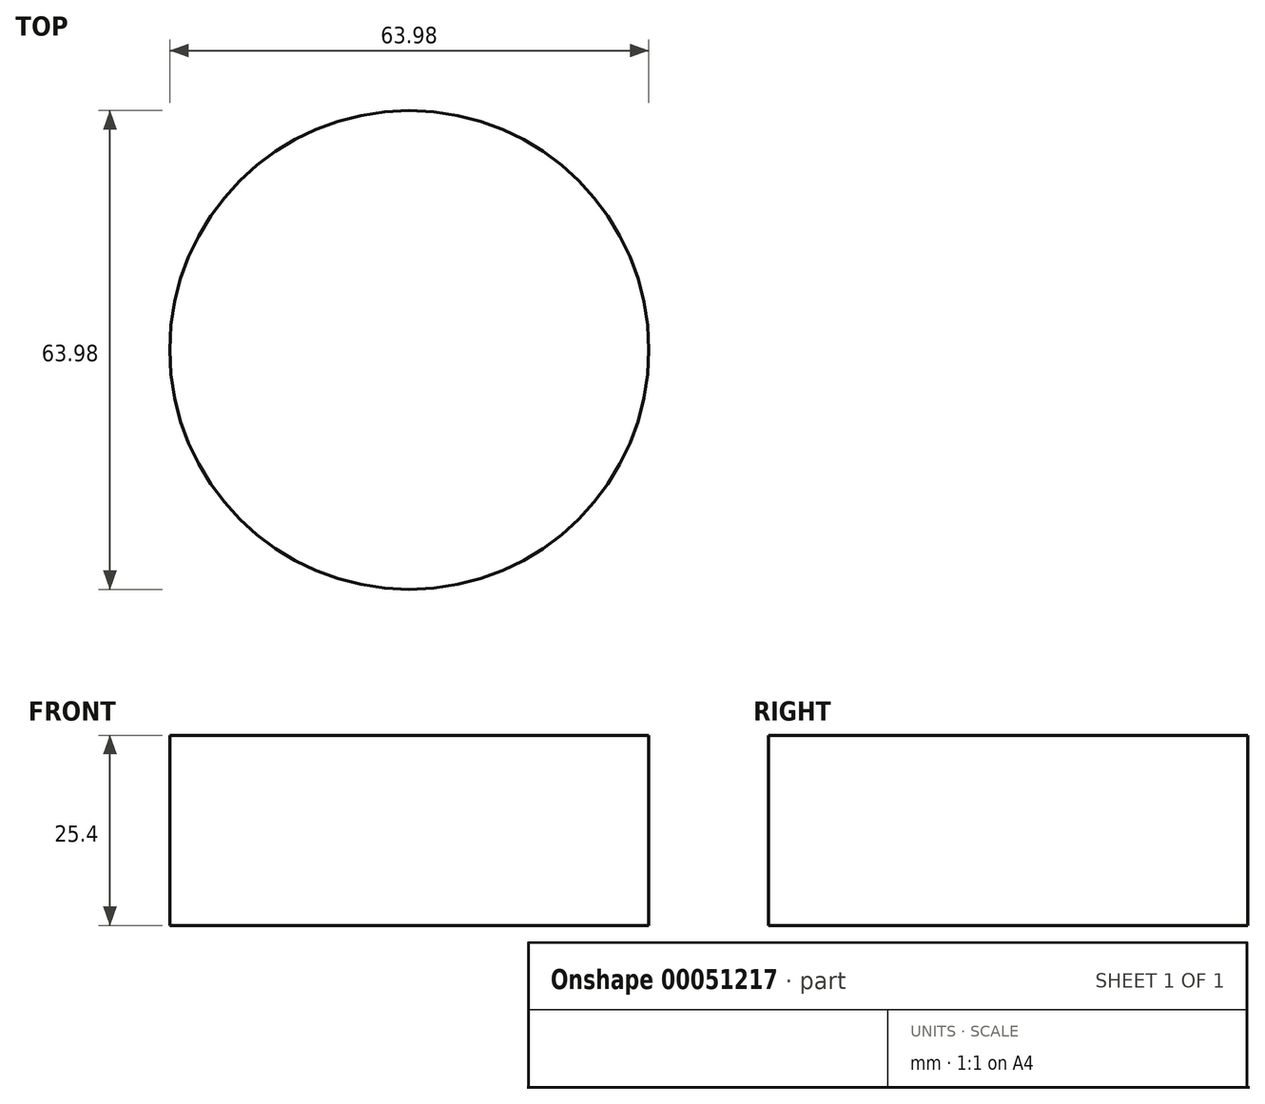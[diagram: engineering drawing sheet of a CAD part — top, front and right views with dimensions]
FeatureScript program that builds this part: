
annotation { "Feature Type Name" : "Feature", "Feature Type Description" : "" }
export const myFeature = defineFeature(function(context is Context, id is Id, definition is map)
    precondition{}
    {
        {
            var Q0;
            Q0=qCreatedBy(makeId("Top.planeOp"),FACE);
            var sketch = newSketch(context, id + "F0", { "sketchPlane" : qUnion([Q0])});
            skCircle(sketch, "E0", {"center": v(0, 0) * mm, "radius": 31.99 * mm});
            skSolve(sketch);
        }
        {
            var Q0;
            Q0 = qSketchRegion(id + "F0", true);
            extrude(context, id + "F1", {"entities" : qUnion([Q0]), "depth" : 25.4 * mm});
        }
    });
